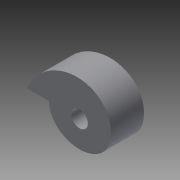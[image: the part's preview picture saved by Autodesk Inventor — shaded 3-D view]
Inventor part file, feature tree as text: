
AUTODESK INVENTOR PART (.ipt)
format: ipt  version: 2014 (Build 180170000, 170)  size: 97,792 bytes
history: native  units: in
note: dims shown in document units (in); Inventor stores cm internally (conversion verified against a paired STEP export)
features: extrude x1, sketch x1
ambient origin geometry x8: Origin, YZ Plane, XZ Plane, XY Plane, X Axis, Y Axis, Z Axis, Center Point
bodies: Solid1 (feature_tree)
feature tree (2):
  extrude  "Extrusion1"  Depth=0.664in
  sketch  "Sketch1"  dims[d18=1.59in d19=0.664in d29=1.6164in d30=1.406in d31=0.9869in d32=1.4075in d33=1.1558in d43=0.8251in d50=0.5in d51=1.0in d52=0.0in d60=0.926in d61=0.7976in d62=0.7134in d63=0.7293in]
